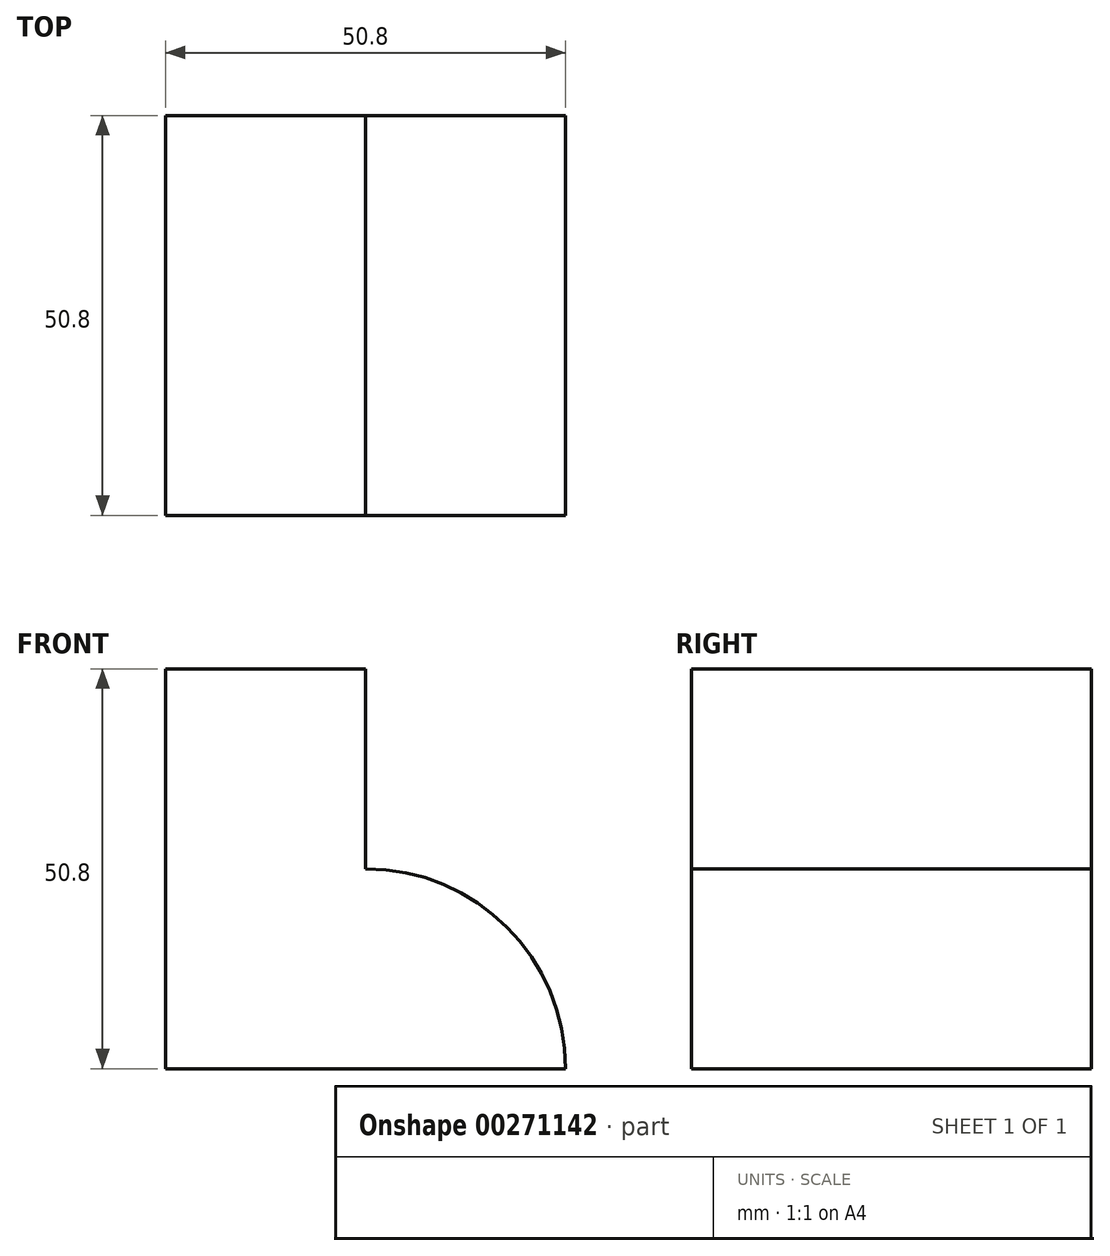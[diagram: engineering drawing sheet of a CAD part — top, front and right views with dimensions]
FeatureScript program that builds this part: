
annotation { "Feature Type Name" : "Feature", "Feature Type Description" : "" }
export const myFeature = defineFeature(function(context is Context, id is Id, definition is map)
    precondition{}
    {
        {
            var Q0;
            Q0=qCreatedBy(makeId("Front.planeOp"),FACE);
            var sketch = newSketch(context, id + "F0", { "sketchPlane" : qUnion([Q0])});
            skLineSegment(sketch, "E0", {"start": v(-44.87, 63.78) * mm, "end": v(-44.87, 12.98) * mm});
            skLineSegment(sketch, "E1", {"start": v(-44.87, 12.98) * mm, "end": v(5.93, 12.98) * mm});
            skLineSegment(sketch, "E2", {"start": v(-19.47, 38.38) * mm, "end": v(-19.47, 63.78) * mm});
            skLineSegment(sketch, "E3", {"start": v(-44.87, 63.78) * mm, "end": v(-19.47, 63.78) * mm});
            skArc(sketch, "E4", {"start": v(5.93, 12.98) * mm, "mid": v(-1.51, 30.95) * mm, "end": v(-19.47, 38.38) * mm});
            skSolve(sketch);
        }
        {
            var Q0;
            Q0 = qSketchRegion(id + "F0", true);
            extrude(context, id + "F1", {"entities" : qUnion([Q0]), "depth" : 50.8 * mm});
        }
    });
